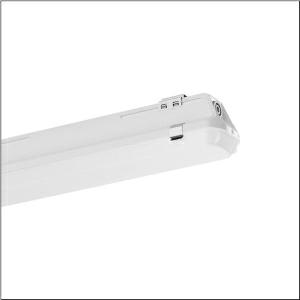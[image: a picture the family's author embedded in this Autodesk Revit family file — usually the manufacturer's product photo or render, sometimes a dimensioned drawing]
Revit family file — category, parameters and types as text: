
# Revit family: monsun_r__21_51fb107l447j3g_a1d1
name_source: partatom
category: Lighting Fixtures
units: mm (PartAtom-declared; Revit-internal decimal feet)

## family parameters
Cut with Voids When Loaded = No
Host = Face
Light Source = No
Part Type = Normal
Room Calculation Point = No
Round Connector Dimension = Use Diameter
Shared = No

## types (1)
- --- (1 x LED, 850 lm, 4.5 W, 4000K)
    Apparent Load = 5 VA
    CIE Flux Codes = 46 76 93 94 100
    Color Rendering = 80
    Color Temperature = 4000K
    Default Elevation = 1800 mm
    Description = Monsun® 21, damp-proof luminaire, chain hanger, primary optical cover: enclosure, of PMMA, light emission: direct distribution, primary light characteristic: symmetric, installation type: suspended mounting, surface-mounted, horizontal mounting, vertical mounting, LED, rated luminous flux: 4.330lm, luminous efficacy: 140lm/W, light colour: 840, colour temperature: 4000K, control gear: ECG, with terminal, 3-pole, max. 2.5mm², mains connection: 220..240V, AC, 50/60Hz, rated input power: 31W, control gear: single battery element, battery: NiCd, 4,5Ah, mains connection: 230V, housing, of glass-fibre reinforced plastic, uncoated, bright grey, incl. chain hanger, length: 1.299mm, width: 90mm, height: 88mm, clip for enclosure, of stainless steel (V2A), ceiling mounting element, of stainless steel (V2A), chain hanger, of stainless steel (V2A), protection rating (complete): IP66, insulation class (complete): insulation class I (protective earthing), certification: CE, UKCA, protection symbol: D, impact resistance: IK04, permissible operating ambient temperature: +5..+25°C, standard: EN 50419, EN 60598-2-1, corresponds to IFS (International Featured Standards) requirements for safety and quality in the food industry, for indoor or canopied outdoor use, no direct snow, no direct sun, no direct rain, contact your sales advisor before using the luminaires in applications with unclear chemical exposure, large temperature fluctuations or condensation-forming humidity, LABS conformity tested according to VDMA 24364:2018-05, packaging unit: 1 piece
    Height = 88 mm
    Lamp = 1 x LED
    Lamp Light Flux = 850 lm
    Lamp Power = 4.5 W
    Lamp count = 1
    Length = 1299 mm
    Luminous efficacy = 189 lm/W
    Manufacturer = Siteco
    ModVariant = No
    Model = 51FB107L447J3G
    Mounting Place = Ceiling
    Mounting Type = Surface mounted
    Number of Poles = 1
    OnlyDefault = Yes
    Power Factor = 1
    Product Name = Monsun® 21
    Product group = damp-proof luminaire
    ProductGroupID = 300
    Protection Class = Protection class I
    Protection Degree = IP 66
    RLX_Detail_Level = 1
    RLX_Emergency_Light_Flux = 0 lm
    RLX_Emergency_Type = 0
    RLX_Emergency_Type_DB = No
    RlxData = <blob elided: 90129 chars, md5=a77f4b5b>
    Socket = socket
    Standby Power = 0 W
    System Light Flux = 850 lm
    System Power = 5 W
    Type Comments = : 3 h
    Type Image = l_1006717.jpg
    URL = http://relux.com
    VarID = @adj_074929
    Voltage = 0 V
    Weight = 0.00 kg
    Width = 90 mm

## geometry (parser evidence)
native form markers: Blend x4, Sweep x12
no freeform markers — native parametric forms only
